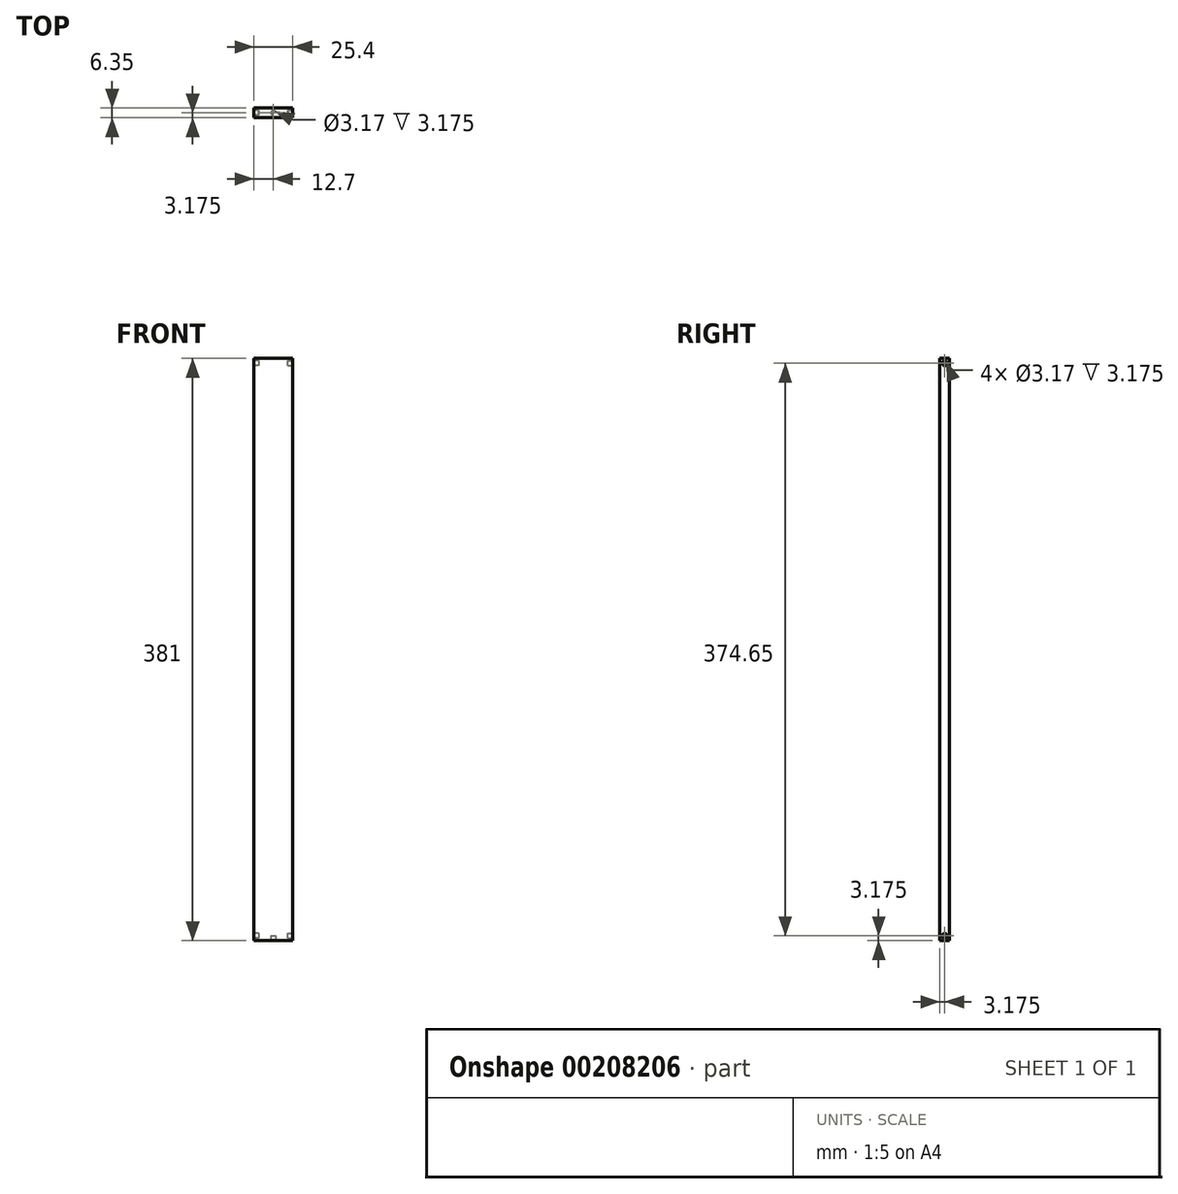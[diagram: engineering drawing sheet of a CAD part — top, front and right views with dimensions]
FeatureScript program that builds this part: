
annotation { "Feature Type Name" : "Feature", "Feature Type Description" : "" }
export const myFeature = defineFeature(function(context is Context, id is Id, definition is map)
    precondition{}
    {
        {
            var Q0;
            Q0=qCreatedBy(makeId("Front.planeOp"),FACE);
            var sketch = newSketch(context, id + "F0", { "sketchPlane" : qUnion([Q0])});
            skLineSegment(sketch, "E0.bottom", {"start": v(-12.7, 190.5) * mm, "end": v(12.7, 190.5) * mm});
            skLineSegment(sketch, "E0.top", {"start": v(-12.7, -190.5) * mm, "end": v(12.7, -190.5) * mm});
            skLineSegment(sketch, "E0.left", {"start": v(-12.7, 190.5) * mm, "end": v(-12.7, -190.5) * mm});
            skLineSegment(sketch, "E0.right", {"start": v(12.7, 190.5) * mm, "end": v(12.7, -190.5) * mm});
            skPoint(sketch, "E0.middle", {"position": v(0, 0) * mm});
            skSolve(sketch);
        }
        {
            var Q0;
            Q0 = qSketchRegion(id + "F0", true);
            extrude(context, id + "F1", {"entities" : qUnion([Q0]), "depth" : 6.35 * mm});
        }
        {
            var Q0;
            Q0=makeQuery(id+"F1.opExtrude","SWEPT_FACE",FACE,{"disambiguationData":[OSD([sQuery(id+"F0.wireOp",EDGE,"E0.right")])]});
            var sketch = newSketch(context, id + "F2", { "sketchPlane" : qUnion([Q0])});
            skLineSegment(sketch, "E1", {"start": v(-6.35, 187.33) * mm, "end": v(0, 187.33) * mm, "construction": true});
            skCircle(sketch, "E2", {"center": v(-3.18, 187.33) * mm, "radius": 1.59 * mm});
            skLineSegment(sketch, "E3", {"start": v(-6.35, -187.32) * mm, "end": v(0, -187.32) * mm, "construction": true});
            skCircle(sketch, "E4", {"center": v(-3.18, -187.32) * mm, "radius": 1.59 * mm});
            skSolve(sketch);
        }
        {
            var Q0;
            Q0 = qSketchRegion(id + "F2", true);
            extrude(context, id + "F3", {"entities" : qUnion([Q0]), "operationType" : NewBodyOperationType.REMOVE, "oppositeDirection" : true, "depth" : 3.17 * mm});
        }
        {
            var Q0;
            Q0=makeQuery(id+"F1.opExtrude","SWEPT_FACE",FACE,{"disambiguationData":[OSD([sQuery(id+"F0.wireOp",EDGE,"E0.left")])]});
            var sketch = newSketch(context, id + "F4", { "sketchPlane" : qUnion([Q0])});
            skLineSegment(sketch, "E5", {"start": v(0, 187.33) * mm, "end": v(6.35, 187.33) * mm, "construction": true});
            skCircle(sketch, "E6", {"center": v(3.18, 187.33) * mm, "radius": 1.59 * mm});
            skLineSegment(sketch, "E7", {"start": v(0, -187.33) * mm, "end": v(6.35, -187.33) * mm, "construction": true});
            skCircle(sketch, "E8", {"center": v(3.18, -187.33) * mm, "radius": 1.59 * mm});
            skSolve(sketch);
        }
        {
            var Q0;
            Q0 = qSketchRegion(id + "F4", true);
            extrude(context, id + "F5", {"entities" : qUnion([Q0]), "operationType" : NewBodyOperationType.REMOVE, "oppositeDirection" : true, "depth" : 3.17 * mm});
        }
        {
            var Q0;
            Q0=makeQuery(id+"F1.opExtrude","SWEPT_FACE",FACE,{"disambiguationData":[OSD([sQuery(id+"F0.wireOp",EDGE,"E0.top")])]});
            var sketch = newSketch(context, id + "F6", { "sketchPlane" : qUnion([Q0])});
            skLineSegment(sketch, "E9", {"start": v(-12.7, 6.35) * mm, "end": v(12.7, 0) * mm, "construction": true});
            skLineSegment(sketch, "E10", {"start": v(-12.7, 0) * mm, "end": v(12.7, 6.35) * mm, "construction": true});
            skCircle(sketch, "E11", {"center": v(0, 3.18) * mm, "radius": 1.59 * mm});
            skSolve(sketch);
        }
        {
            var Q0;
            Q0 = qSketchRegion(id + "F6", true);
            extrude(context, id + "F7", {"entities" : qUnion([Q0]), "operationType" : NewBodyOperationType.REMOVE, "oppositeDirection" : true, "depth" : 3.17 * mm});
        }
    });
